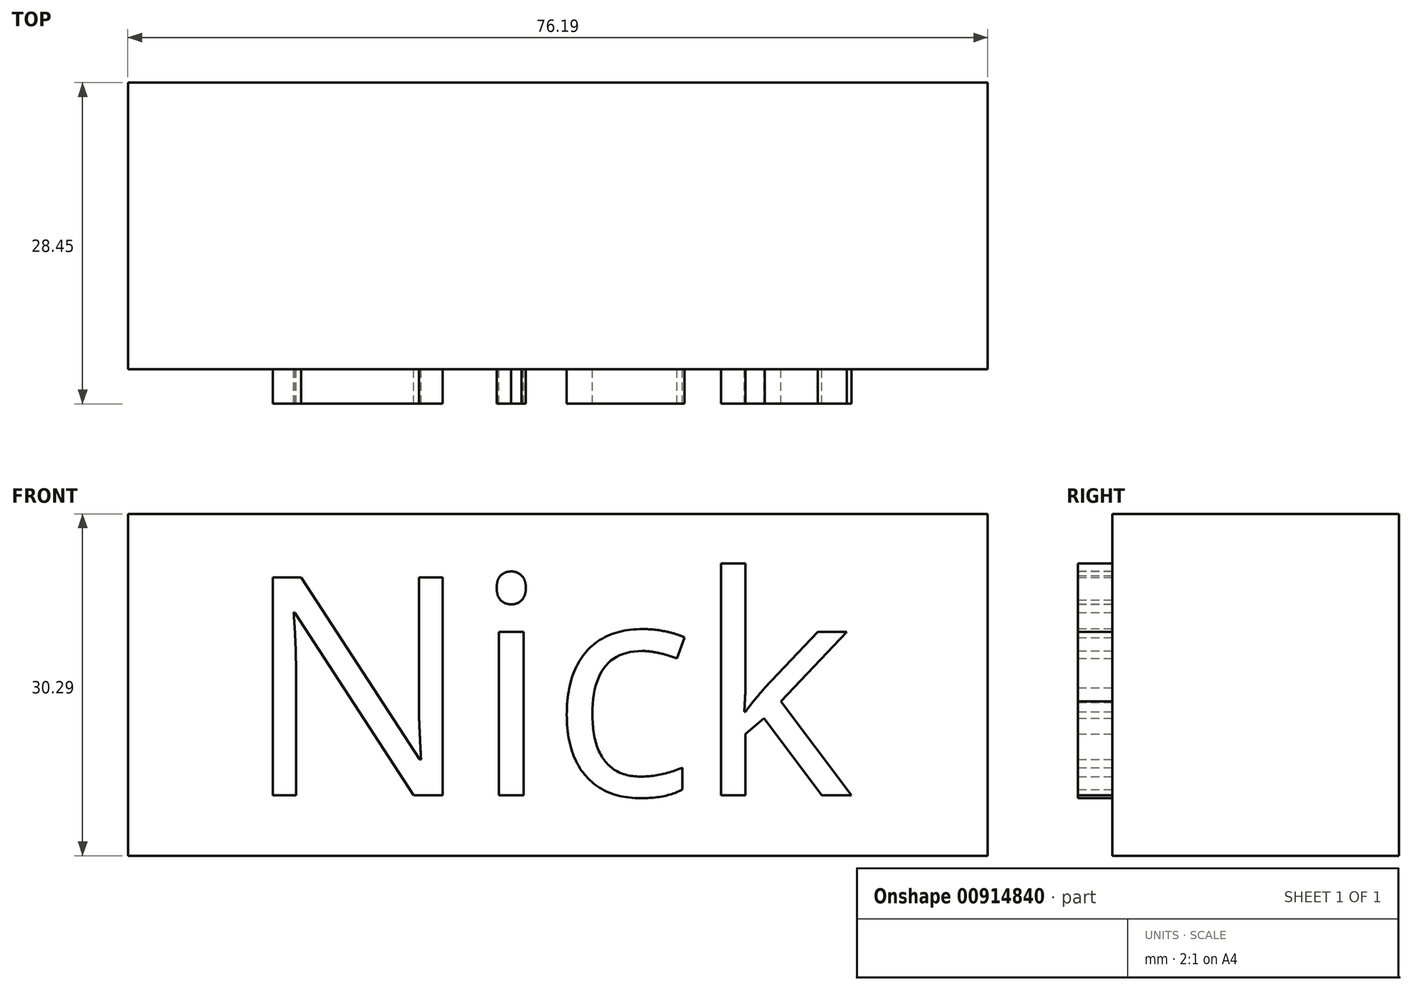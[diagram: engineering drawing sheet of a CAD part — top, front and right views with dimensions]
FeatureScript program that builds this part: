
annotation { "Feature Type Name" : "Feature", "Feature Type Description" : "" }
export const myFeature = defineFeature(function(context is Context, id is Id, definition is map)
    precondition{}
    {
        {
            var Q0;
            Q0=qCreatedBy(makeId("Front.planeOp"),FACE);
            var sketch = newSketch(context, id + "F0", { "sketchPlane" : qUnion([Q0])});
            skLineSegment(sketch, "E0.bottom", {"start": v(-27.38, 54.5) * mm, "end": v(48.8, 54.5) * mm});
            skLineSegment(sketch, "E0.top", {"start": v(-27.38, 24.2) * mm, "end": v(48.8, 24.2) * mm});
            skLineSegment(sketch, "E0.left", {"start": v(-27.38, 54.5) * mm, "end": v(-27.38, 24.2) * mm});
            skLineSegment(sketch, "E0.right", {"start": v(48.8, 54.5) * mm, "end": v(48.8, 24.2) * mm});
            skSolve(sketch);
        }
        {
            var Q0;
            Q0 = qSketchRegion(id + "F0", true);
            extrude(context, id + "F1", {"entities" : qUnion([Q0]), "depth" : 25.4 * mm, "offsetDistance" : 25.4 * mm});
        }
        {
            var Q0;
            Q0=makeQuery(id+"F1.opExtrude","CAP_FACE",FACE,{"disambiguationData":[OSD([sQuery(id+"F0.wireOp",EDGE,"E0.bottom"),sQuery(id+"F0.wireOp",EDGE,"E0.top"),sQuery(id+"F0.wireOp",EDGE,"E0.left"),sQuery(id+"F0.wireOp",EDGE,"E0.right")])],"isStart":false});
            var sketch = newSketch(context, id + "F2", { "sketchPlane" : qUnion([Q0])});
            skText(sketch, "E1", { "text": "Nick", "fontName": "OpenSans-Regular.ttf"});
            const initialGuessF2  = {"E1": [-0.0172, 0.02956, 1, 0, 0.01945]};
            skSetInitialGuess(sketch, initialGuessF2);
            skSolve(sketch);
        }
        {
            var Q0;
            Q0 = qSketchRegion(id + "F2", true);
            extrude(context, id + "F3", {"entities" : qUnion([Q0]), "operationType" : NewBodyOperationType.ADD, "depth" : 3.05 * mm, "offsetDistance" : 25.4 * mm});
        }
    });
